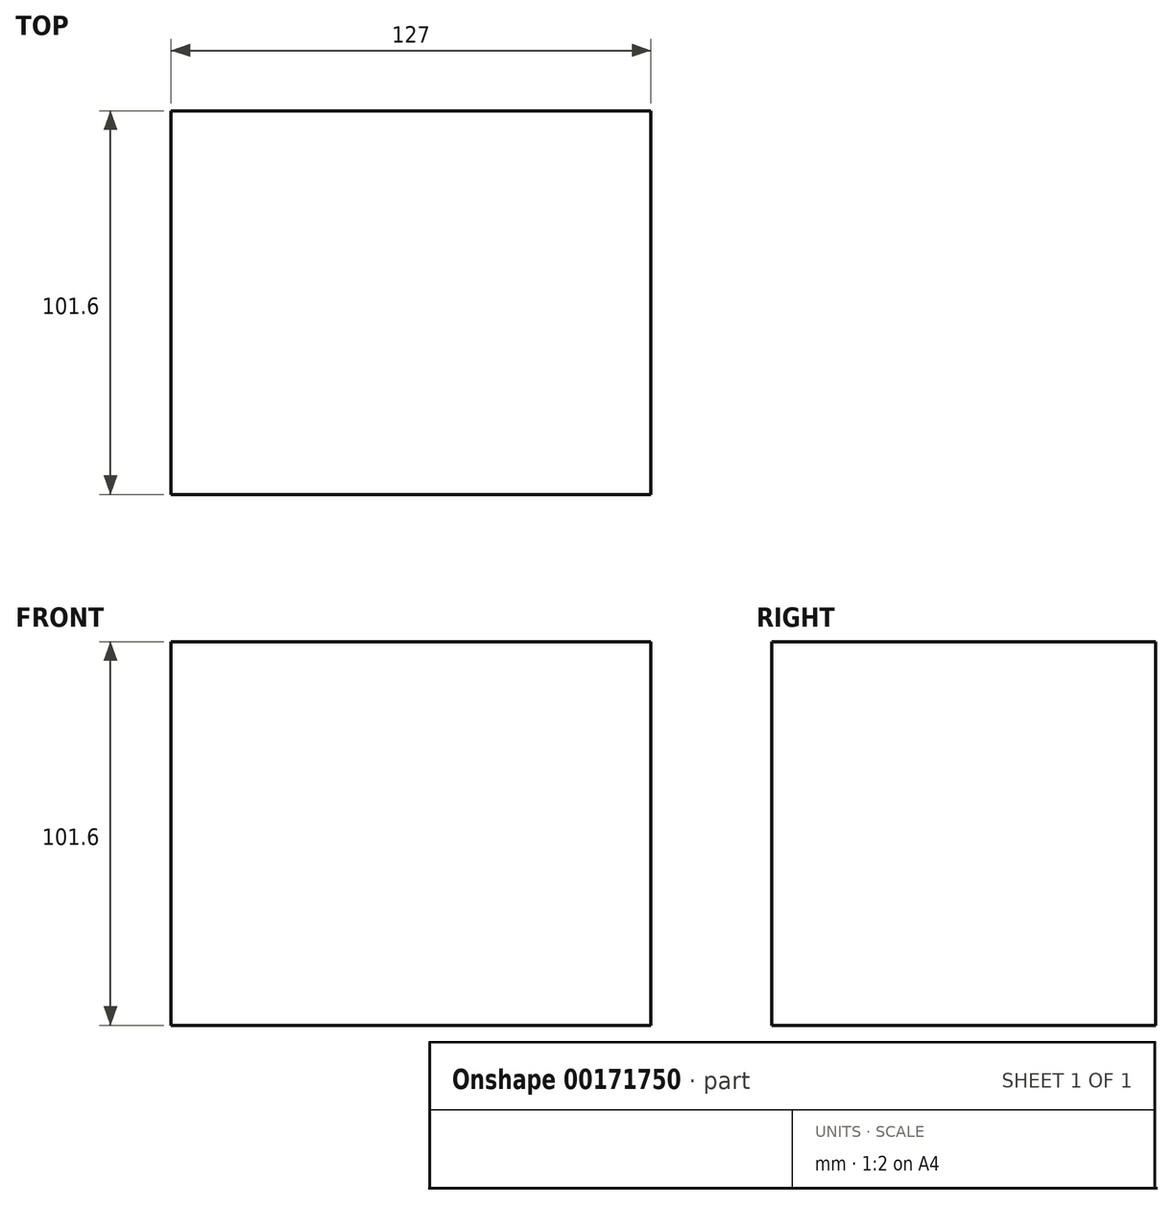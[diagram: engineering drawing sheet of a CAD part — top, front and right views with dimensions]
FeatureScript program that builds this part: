
annotation { "Feature Type Name" : "Feature", "Feature Type Description" : "" }
export const myFeature = defineFeature(function(context is Context, id is Id, definition is map)
    precondition{}
    {
        {
            var Q0;
            Q0=qCreatedBy(makeId("Top.planeOp"),FACE);
            var sketch = newSketch(context, id + "F0", { "sketchPlane" : qUnion([Q0])});
            skLineSegment(sketch, "E0.bottom", {"start": v(0, 0) * mm, "end": v(127, 0) * mm});
            skLineSegment(sketch, "E0.top", {"start": v(0, -101.6) * mm, "end": v(127, -101.6) * mm});
            skLineSegment(sketch, "E0.left", {"start": v(0, 0) * mm, "end": v(0, -101.6) * mm});
            skLineSegment(sketch, "E0.right", {"start": v(127, 0) * mm, "end": v(127, -101.6) * mm});
            skSolve(sketch);
        }
        {
            var Q0;
            Q0 = qSketchRegion(id + "F0", true);
            extrude(context, id + "F1", {"entities" : qUnion([Q0]), "depth" : 101.6 * mm});
        }
    });
